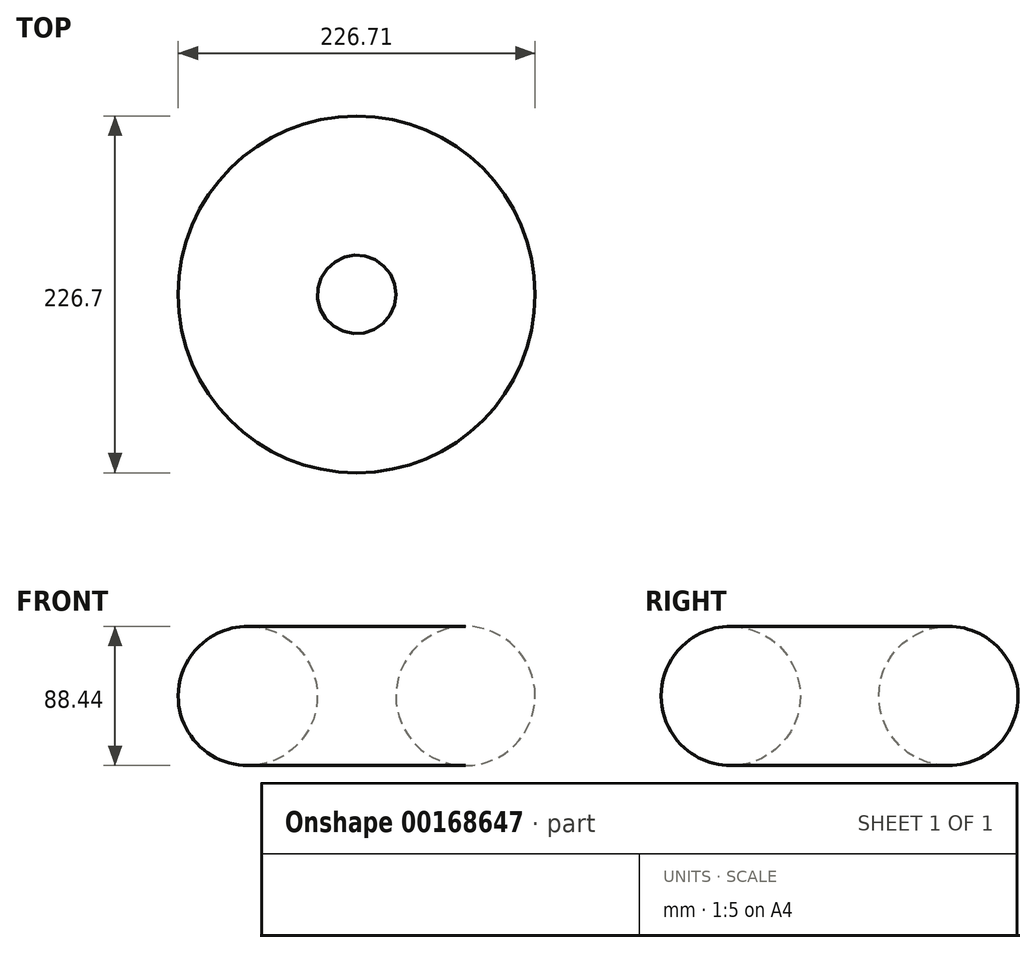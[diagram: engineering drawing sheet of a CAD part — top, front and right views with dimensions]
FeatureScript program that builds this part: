
annotation { "Feature Type Name" : "Feature", "Feature Type Description" : "" }
export const myFeature = defineFeature(function(context is Context, id is Id, definition is map)
    precondition{}
    {
        {
            var Q0;
            Q0=qCreatedBy(makeId("Front.planeOp"),FACE);
            var sketch = newSketch(context, id + "F0", { "sketchPlane" : qUnion([Q0])});
            skCircle(sketch, "E0", {"center": v(-13.86, 12.07) * mm, "radius": 44.22 * mm});
            skLineSegment(sketch, "E1", {"start": v(55.28, 52.6) * mm, "end": v(55.28, -29.35) * mm, "construction": true});
            skSolve(sketch);
        }
        {
            var Q0;
            Q0=makeQuery(id+"F0.imprint","IMPRINT",FACE,{"disambiguationData":[TD([[makeQuery(id+"F0.imprint","IMPRINT",EDGE,{"derivedFrom":sQuery(id+"F0.wireOp",EDGE,"E0")}),1.0]])]});
            var Q1;
            Q1=sQuery(id+"F0.wireOp",EDGE,"E1");
            revolve(context, id + "F1", {"entities" : qUnion([Q0]), "axis" : qUnion([Q1]), "revolveType" : RevolveType.FULL});
        }
    });
